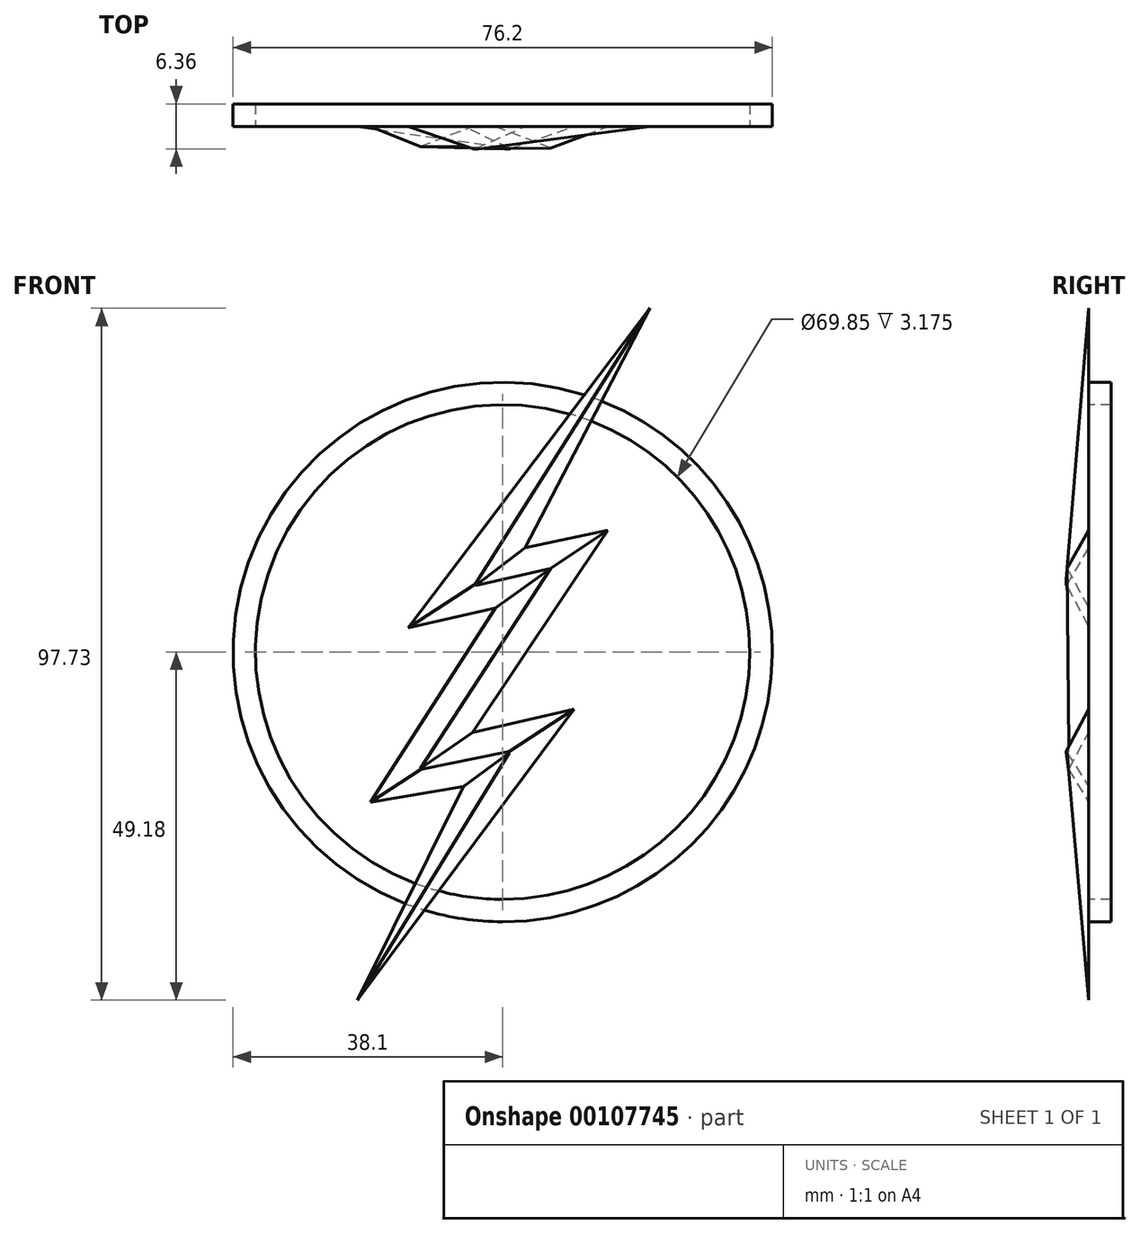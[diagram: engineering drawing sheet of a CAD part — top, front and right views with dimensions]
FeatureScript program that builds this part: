
annotation { "Feature Type Name" : "Feature", "Feature Type Description" : "" }
export const myFeature = defineFeature(function(context is Context, id is Id, definition is map)
    precondition{}
    {
        {
            var Q0;
            Q0=qCreatedBy(makeId("Front.planeOp"),FACE);
            var sketch = newSketch(context, id + "F0", { "sketchPlane" : qUnion([Q0])});
            skCircle(sketch, "E0", {"center": v(0, 0) * mm, "radius": 38.1 * mm});
            skCircle(sketch, "E1.0", {"center": v(0, 0) * mm, "radius": 34.93 * mm});
            skSolve(sketch);
        }
        {
            var Q0;
            Q0=makeQuery(id+"F0.imprint","IMPRINT",FACE,{"disambiguationData":[TD([[makeQuery(id+"F0.imprint","IMPRINT",EDGE,{"derivedFrom":sQuery(id+"F0.wireOp",EDGE,"E0")}),1.0]])]});
            extrude(context, id + "F1", {"entities" : qUnion([Q0]), "oppositeDirection" : true, "depth" : 3.17 * mm});
        }
        {
            var Q0;
            Q0=qCreatedBy(makeId("Front.planeOp"),FACE);
            var sketch = newSketch(context, id + "F2", { "sketchPlane" : qUnion([Q0])});
            skLineSegment(sketch, "E2", {"start": v(20.81, 48.55) * mm, "end": v(-13.36, 3.44) * mm});
            skLineSegment(sketch, "E3", {"start": v(20.81, 48.55) * mm, "end": v(3.14, 14.7) * mm});
            skLineSegment(sketch, "E4", {"start": v(3.14, 14.7) * mm, "end": v(14.83, 17.23) * mm});
            skLineSegment(sketch, "E5", {"start": v(14.83, 17.23) * mm, "end": v(-4.25, -11.35) * mm});
            skLineSegment(sketch, "E6", {"start": v(-4.25, -11.35) * mm, "end": v(10.08, -8.07) * mm});
            skLineSegment(sketch, "E7", {"start": v(10.08, -8.07) * mm, "end": v(-20.51, -49.18) * mm});
            skLineSegment(sketch, "E8", {"start": v(-13.36, 3.44) * mm, "end": v(-1.06, 6.25) * mm});
            skLineSegment(sketch, "E9", {"start": v(-1.06, 6.25) * mm, "end": v(-18.67, -21.24) * mm});
            skLineSegment(sketch, "E10", {"start": v(-18.67, -21.24) * mm, "end": v(-5.51, -19.01) * mm});
            skLineSegment(sketch, "E11", {"start": v(-5.51, -19.01) * mm, "end": v(-20.51, -49.18) * mm});
            skPoint(sketch, "E12", {"position": v(-10.95, -15.7) * mm});
            skPoint(sketch, "E13", {"position": v(2.06, -13.67) * mm});
            skPoint(sketch, "E14", {"position": v(5.45, 10.7) * mm});
            skPoint(sketch, "E15", {"position": v(-5.04, 8.9) * mm});
            skLineSegment(sketch, "E16", {"start": v(-5.04, 8.9) * mm, "end": v(5.45, 10.7) * mm});
            skLineSegment(sketch, "E17", {"start": v(-10.95, -15.7) * mm, "end": v(2.06, -13.67) * mm});
            skLineSegment(sketch, "E18", {"start": v(-5.04, 8.9) * mm, "end": v(20.81, 48.55) * mm});
            skLineSegment(sketch, "E19", {"start": v(5.45, 10.7) * mm, "end": v(-10.95, -15.7) * mm});
            skLineSegment(sketch, "E20", {"start": v(2.06, -13.67) * mm, "end": v(-20.51, -49.18) * mm});
            skLineSegment(sketch, "E21", {"start": v(-5.04, 8.9) * mm, "end": v(-13.36, 3.44) * mm});
            skLineSegment(sketch, "E22", {"start": v(3.14, 14.7) * mm, "end": v(-5.04, 8.9) * mm});
            skLineSegment(sketch, "E23", {"start": v(5.45, 10.7) * mm, "end": v(14.83, 17.23) * mm});
            skLineSegment(sketch, "E24", {"start": v(-1.06, 6.25) * mm, "end": v(5.45, 10.7) * mm});
            skLineSegment(sketch, "E25", {"start": v(-10.95, -15.7) * mm, "end": v(-4.25, -11.35) * mm});
            skLineSegment(sketch, "E26", {"start": v(2.06, -13.67) * mm, "end": v(10.08, -8.07) * mm});
            skLineSegment(sketch, "E27", {"start": v(-5.51, -19.01) * mm, "end": v(2.06, -13.67) * mm});
            skLineSegment(sketch, "E28", {"start": v(-10.95, -15.7) * mm, "end": v(-18.67, -21.24) * mm});
            skSolve(sketch);
        }
        {
            var Q0;
            Q0=qSketchRegion(id+"F2",true);
            extrude(context, id + "F3", {"entities" : qUnion([Q0]), "depth" : 3.17 * mm, "hasDraft" : true, "draftAngle" : 50 * degree, "draftPullDirection" : true});
        }
    });
